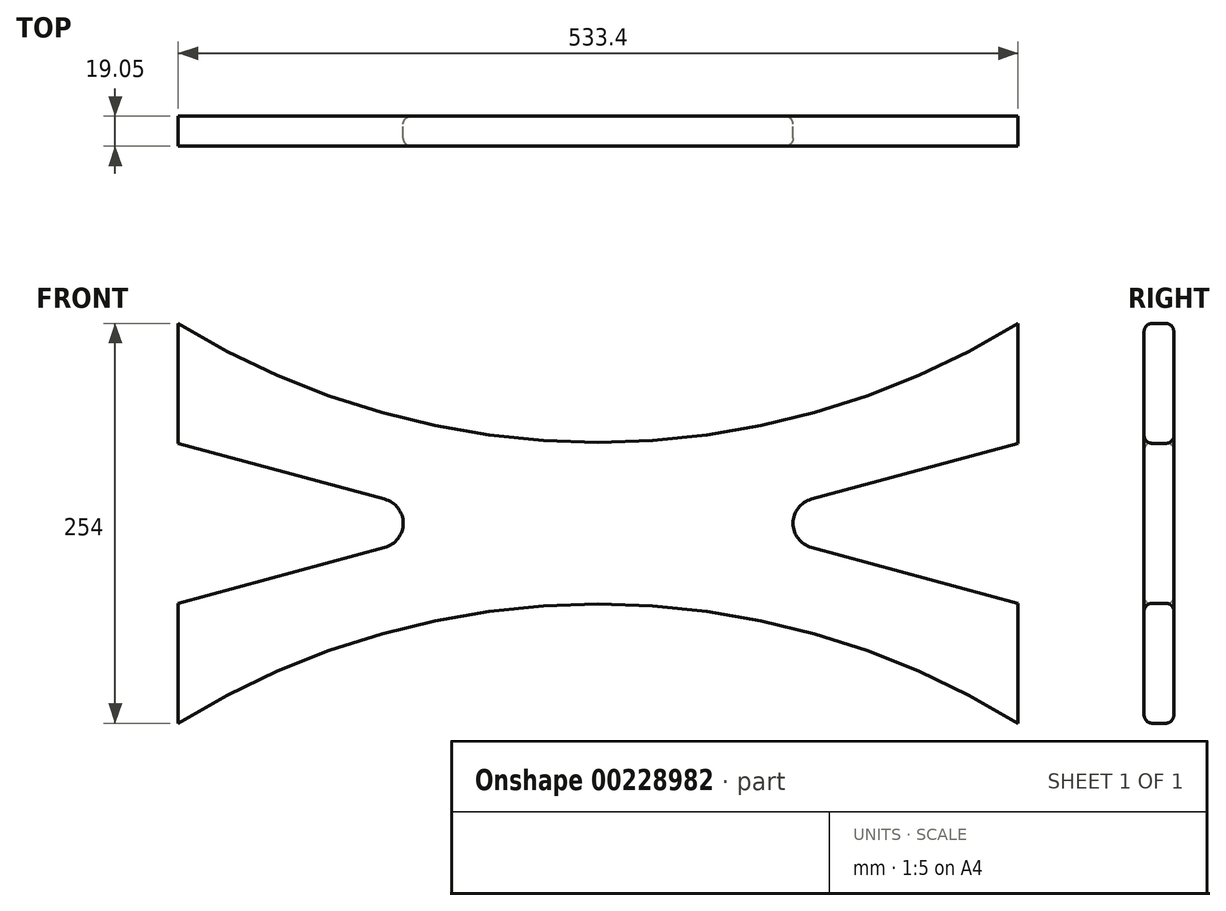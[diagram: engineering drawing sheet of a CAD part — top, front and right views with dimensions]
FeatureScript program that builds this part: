
annotation { "Feature Type Name" : "Feature", "Feature Type Description" : "" }
export const myFeature = defineFeature(function(context is Context, id is Id, definition is map)
    precondition{}
    {
        {
            var Q0;
            Q0=qCreatedBy(makeId("Front.planeOp"),FACE);
            var sketch = newSketch(context, id + "F0", { "sketchPlane" : qUnion([Q0])});
            skPoint(sketch, "E0.middle", {"position": v(0, 0) * mm});
            skLineSegment(sketch, "E1", {"start": v(266.7, 50.8) * mm, "end": v(266.7, 127) * mm});
            skLineSegment(sketch, "E2", {"start": v(-266.7, 127) * mm, "end": v(-266.7, 50.8) * mm});
            skLineSegment(sketch, "E3", {"start": v(266.7, -50.8) * mm, "end": v(266.7, -127) * mm});
            skLineSegment(sketch, "E4", {"start": v(-266.7, -127) * mm, "end": v(-266.7, -50.8) * mm});
            skArc(sketch, "E5", {"start": v(135.55, 15.32) * mm, "mid": v(123.83, 0) * mm, "end": v(135.55, -15.32) * mm});
            skArc(sketch, "E6", {"start": v(-135.55, -15.32) * mm, "mid": v(-123.83, 0) * mm, "end": v(-135.55, 15.32) * mm});
            skLineSegment(sketch, "E7", {"start": v(266.7, 50.8) * mm, "end": v(135.55, 15.32) * mm});
            skLineSegment(sketch, "E8", {"start": v(266.7, -50.8) * mm, "end": v(135.55, -15.32) * mm});
            skLineSegment(sketch, "E9", {"start": v(-266.7, 50.8) * mm, "end": v(-135.55, 15.32) * mm});
            skLineSegment(sketch, "E10", {"start": v(-266.7, -50.8) * mm, "end": v(-135.55, -15.32) * mm});
            skArc(sketch, "E11", {"start": v(266.7, -127) * mm, "mid": v(0, -51.36) * mm, "end": v(-266.7, -127) * mm});
            skArc(sketch, "E12", {"start": v(-266.7, 127) * mm, "mid": v(0, 51.36) * mm, "end": v(266.7, 127) * mm});
            skSolve(sketch);
        }
        {
            var Q0;
            Q0 = qSketchRegion(id + "F0", true);
            extrude(context, id + "F1", {"entities" : qUnion([Q0]), "depth" : 19.05 * mm});
        }
        {
            var Q0;
            Q0=makeQuery(id+"F1.opExtrude","CAP_EDGE",EDGE,{"disambiguationData":[OSD([sQuery(id+"F0.wireOp",EDGE,"E12")])],"isStart":true});
            var Q1;
            Q1=makeQuery(id+"F1.opExtrude","CAP_EDGE",EDGE,{"disambiguationData":[OSD([sQuery(id+"F0.wireOp",EDGE,"E7")])],"isStart":true});
            var Q2;
            Q2=makeQuery(id+"F1.opExtrude","CAP_EDGE",EDGE,{"disambiguationData":[OSD([sQuery(id+"F0.wireOp",EDGE,"E10")])],"isStart":true});
            var Q3;
            Q3=makeQuery(id+"F1.opExtrude","CAP_EDGE",EDGE,{"disambiguationData":[OSD([sQuery(id+"F0.wireOp",EDGE,"E11")])],"isStart":true});
            fillet(context, id + "F2", {"entities" : qUnion([Q0, Q1, Q2, Q3]), "radius" : 5.08 * mm, "tangentPropagation" : true, "allowEdgeOverflow" : false});
        }
        {
            var Q0;
            Q0=makeQuery(id+"F1.opExtrude","CAP_EDGE",EDGE,{"disambiguationData":[OSD([sQuery(id+"F0.wireOp",EDGE,"E12")])],"isStart":false});
            var Q1;
            Q1=makeQuery(id+"F1.opExtrude","CAP_EDGE",EDGE,{"disambiguationData":[OSD([sQuery(id+"F0.wireOp",EDGE,"E9")])],"isStart":false});
            var Q2;
            Q2=makeQuery(id+"F1.opExtrude","CAP_EDGE",EDGE,{"disambiguationData":[OSD([sQuery(id+"F0.wireOp",EDGE,"E11")])],"isStart":false});
            var Q3;
            {var subQ0=sQuery(id+"F0.wireOp",EDGE,"E8");Q3=makeQuery(id+"F2.opFillet","BLEND_EDGE",EDGE,{"blendedFrom":[makeQuery(id+"F1.opExtrude","CAP_EDGE",EDGE,{"disambiguationData":[OSD([subQ0])],"isStart":true}),makeQuery(id+"F1.opExtrude","SWEPT_FACE",FACE,{"disambiguationData":[OSD([subQ0])]})],"blendedInto":[makeQuery(id+"F1.opExtrude","SWEPT_FACE",FACE,{"disambiguationData":[OSD([subQ0])]})]});}
            var Q4;
            Q4=makeQuery(id+"F1.opExtrude","CAP_EDGE",EDGE,{"disambiguationData":[OSD([sQuery(id+"F0.wireOp",EDGE,"E7")])],"isStart":false});
            fillet(context, id + "F3", {"entities" : qUnion([Q0, Q1, Q2, Q3, Q4]), "radius" : 5.08 * mm, "tangentPropagation" : true, "allowEdgeOverflow" : false});
        }
    });
